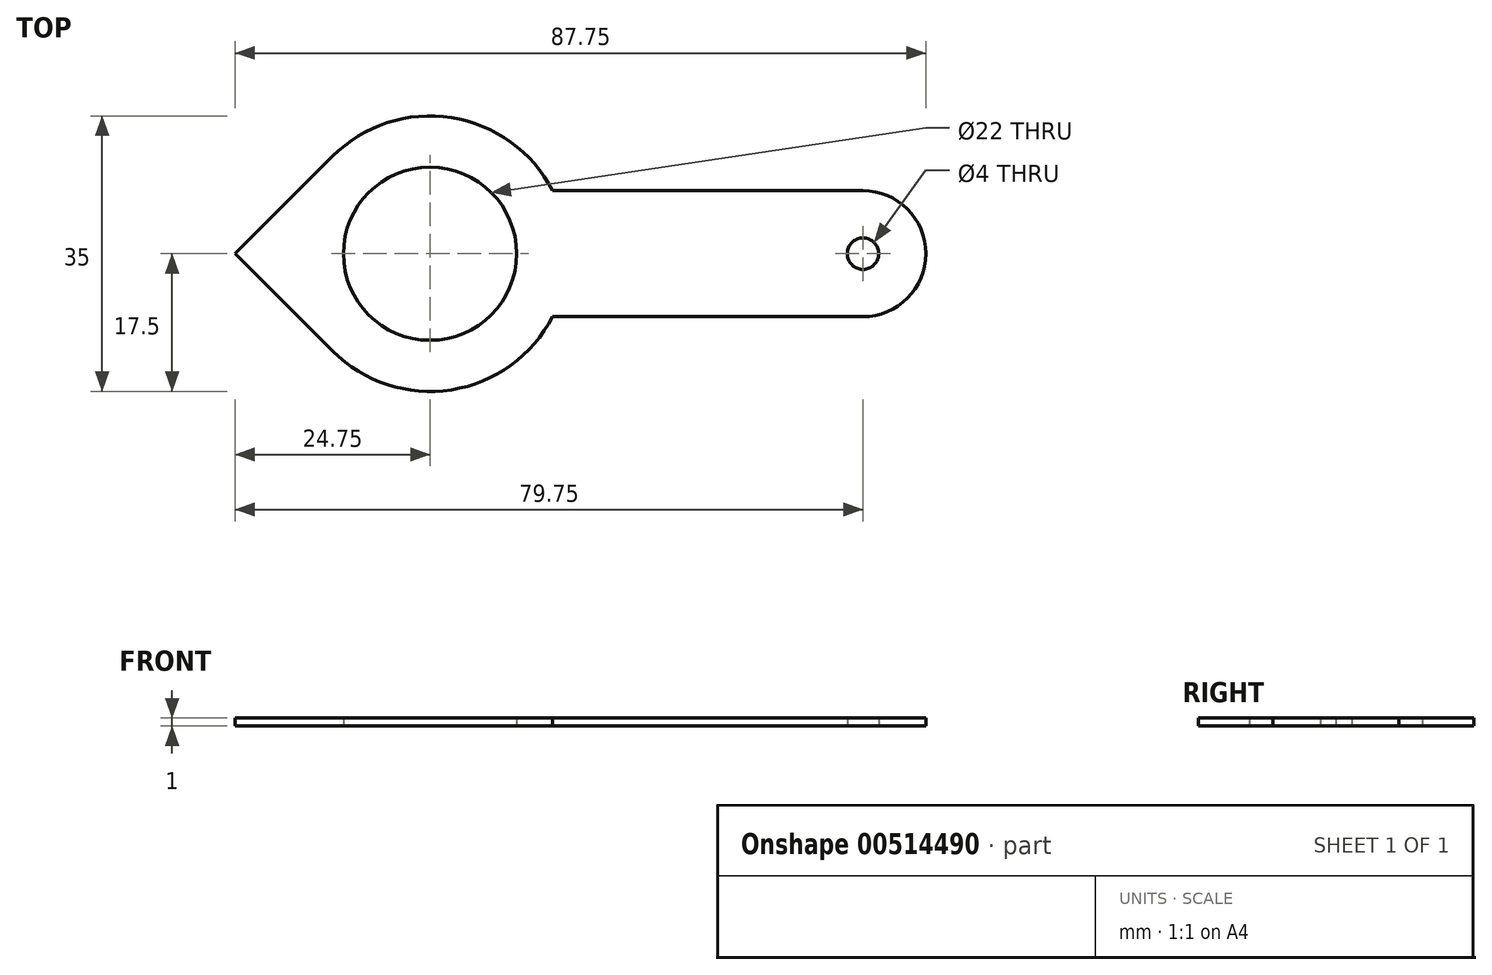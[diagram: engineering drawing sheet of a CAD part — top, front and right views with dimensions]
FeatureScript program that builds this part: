
annotation { "Feature Type Name" : "Feature", "Feature Type Description" : "" }
export const myFeature = defineFeature(function(context is Context, id is Id, definition is map)
    precondition{}
    {
        {
            var Q0;
            Q0=qCreatedBy(makeId("Top.planeOp"),FACE);
            var sketch = newSketch(context, id + "F0", { "sketchPlane" : qUnion([Q0])});
            skCircle(sketch, "E0", {"center": v(0, 0) * mm, "radius": 2 * mm});
            skCircle(sketch, "E1", {"center": v(0, 0) * mm, "radius": 8 * mm});
            skCircle(sketch, "E2", {"center": v(-55, 0) * mm, "radius": 17.5 * mm});
            skLineSegment(sketch, "E3", {"start": v(-79.75, 0) * mm, "end": v(-67.37, 12.37) * mm});
            skLineSegment(sketch, "E4.MirrorCS", {"start": v(-79.75, 0) * mm, "end": v(-67.37, -12.37) * mm});
            skLineSegment(sketch, "E5", {"start": v(0, 8) * mm, "end": v(-39.44, 8) * mm});
            skLineSegment(sketch, "E6.MirrorCS", {"start": v(0, -8) * mm, "end": v(-39.44, -8) * mm});
            skCircle(sketch, "E7", {"center": v(-55, 0) * mm, "radius": 11 * mm});
            skSolve(sketch);
        }
        {
            var Q0;
            {var subQ0=sQuery(id+"F0.wireOp",EDGE,"E2");var subQ1=makeQuery(id+"F0.imprint","INTERSECT",VERTEX,{"derivedFrom":[subQ0,sQuery(id+"F0.wireOp",EDGE,"E3")]});Q0=makeQuery(id+"F0.imprint","IMPRINT",FACE,{"disambiguationData":[TD([[makeQuery(id+"F0.imprint","IMPRINT",EDGE,{"disambiguationData":[TD([[subQ1,1.0]])],"derivedFrom":subQ0}),1.0]])]});}
            var Q1;
            {var subQ0=sQuery(id+"F0.wireOp",EDGE,"E3");Q1=makeQuery(id+"F0.imprint","IMPRINT",FACE,{"disambiguationData":[TD([[makeQuery(id+"F0.imprint","IMPRINT",EDGE,{"derivedFrom":subQ0}),-1.0]])]});}
            var Q2;
            {var subQ0=sQuery(id+"F0.wireOp",EDGE,"E5");Q2=makeQuery(id+"F0.imprint","IMPRINT",FACE,{"disambiguationData":[TD([[makeQuery(id+"F0.imprint","IMPRINT",EDGE,{"derivedFrom":subQ0}),1.0]])]});}
            var Q3;
            Q3=makeQuery(id+"F0.imprint","IMPRINT",FACE,{"disambiguationData":[TD([[makeQuery(id+"F0.imprint","IMPRINT",EDGE,{"derivedFrom":sQuery(id+"F0.wireOp",EDGE,"E0")}),-1.0]])]});
            extrude(context, id + "F1", {"entities" : qUnion([Q0, Q1, Q2, Q3]), "depth" : 1 * mm});
        }
    });
